# Revit family: Haworth_JiveTable_PebbleSymmetricalDiscBase
name_source: partatom
category: Furniture Systems
revit_build: Autodesk Revit 2018 (Build: 20170223_1515(x64)
units: mm (PartAtom-declared; Revit-internal decimal feet)

## family parameters
Always vertical = Yes
Cut with Voids When Loaded = No
OmniClass Number = 23.40.70.14.64.21
OmniClass Title = Systems Furniture
Part Type = Normal
Room Calculation Point = No
Round Connector Dimension = Use Diameter
Shared = No
Work Plane-Based = No

## types (7) — shared parameters
Assembly Code = E2020200
Base Distance = 0"
Custom Size = No
Manufacturer = Haworth, Inc.
Max. Height = 36"
Min. Height = 29"
Model = Haworth Jive
One Disk = Yes
Revision Number = 0
Size = Verify Final Dim. w/ Haworth
Standard Depths = 24, 30, 36, 42 in
Standard Height = 29, 36 in.
Standard Width = 24, 30, 36, 42 in.
Table Thickness = 1 3/16"
URL = http://www.haworth.com
URL - Product = http://www.haworth.com
Warranty = http://www.haworth.com

## per-type parameters (varying)
| type | 24in x 24in | 30in x 30in | 36in x 36in | 42in x 42in | Actual Depth | Actual Height | Actual Width | Description | Disc Distance | Height | Leg Height |
| 24d 24w 29h | Yes | No | No | No | 24" | 29" | 24" | Haworth Jive Table Pebble Symmetrical Disc Base - 24d 24w 29h | 8 1/2" | 29" | 27 13/16" |
| 30d 30w 29h | No | Yes | No | No | 30" | 29" | 30" | Haworth Jive Table Pebble Symmetrical Disc Base - 30d 30w 29h | 11" | 29" | 27 13/16" |
| 36d 36w 29h | No | No | Yes | No | 36" | 29" | 36" | Haworth Jive Table Pebble Symmetrical Disc Base - 36d 36w 29h | 13 1/2" | 29" | 27 13/16" |
| 42d 42w 29h | No | No | No | Yes | 42" | 29" | 42" | Haworth Jive Table Pebble Symmetrical Disc Base - 42d 42w 29h | 13 1/2" | 29" | 27 13/16" |
| 30d 30w 36h | No | Yes | No | No | 30" | 36" | 30" | Haworth Jive Table Pebble Symmetrical Disc Base - 30d 30w 36h | 11" | 36" | 34 13/16" |
| 36d 36w 36h | No | No | Yes | No | 36" | 36" | 36" | Haworth Jive Table Pebble Symmetrical Disc Base - 36d 36w 36h | 13 1/2" | 36" | 34 13/16" |
| 42d 42w 36h | No | No | No | Yes | 42" | 36" | 42" | Haworth Jive Table Pebble Symmetrical Disc Base - 42d 42w 36h | 13 1/2" | 36" | 34 13/16" |

## geometry (parser evidence)
native form markers: Sweep x8
no freeform markers — native parametric forms only
